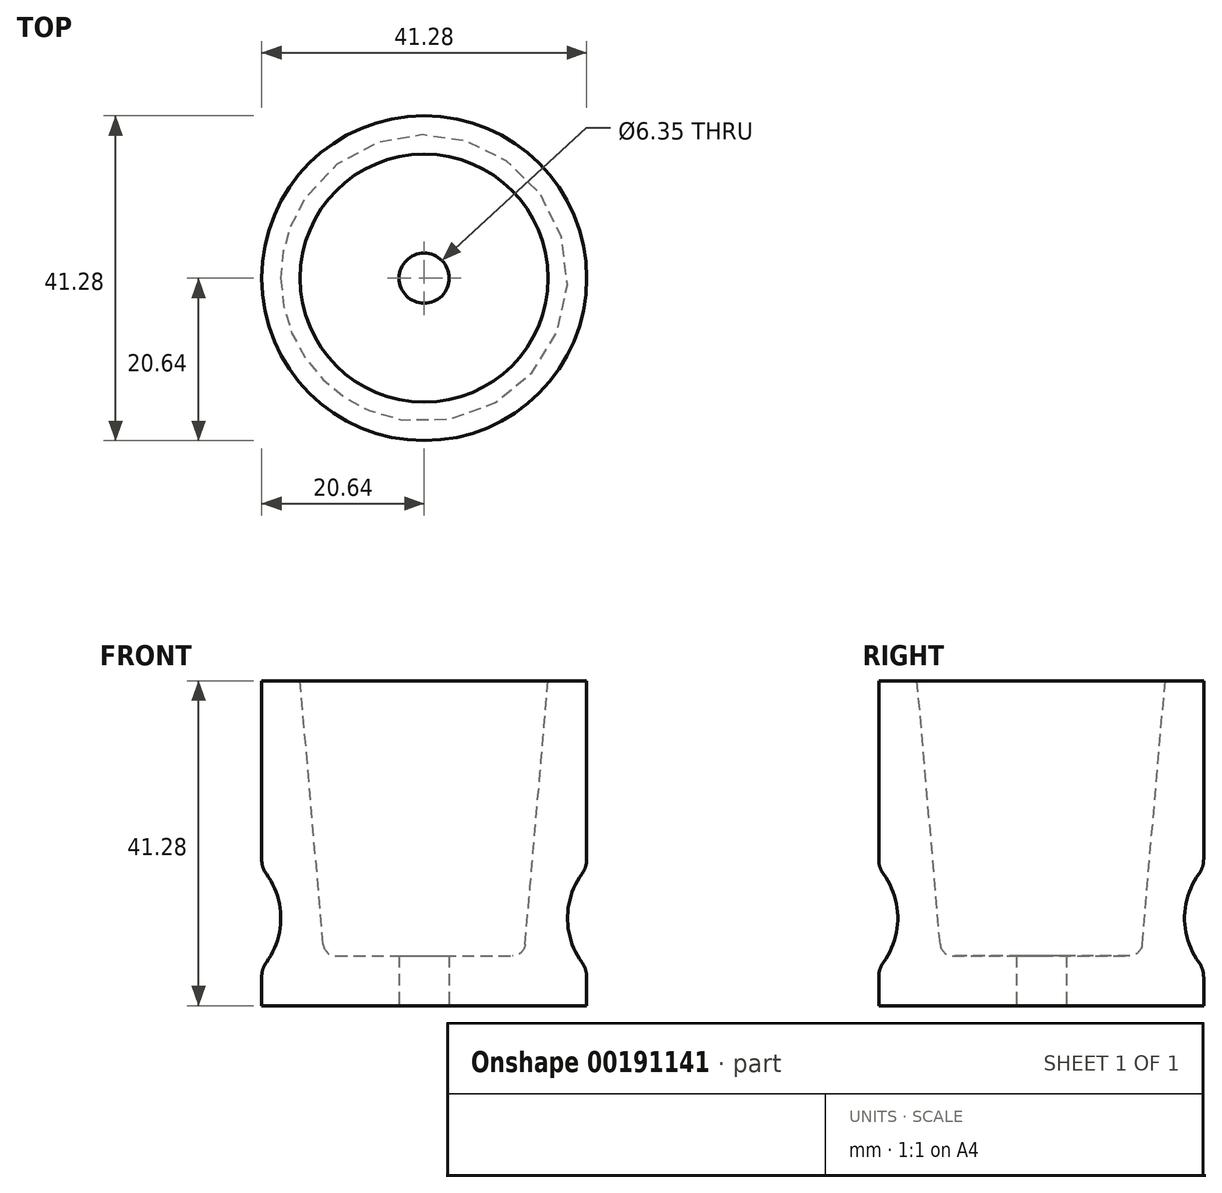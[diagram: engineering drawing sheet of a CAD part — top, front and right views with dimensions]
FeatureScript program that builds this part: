
annotation { "Feature Type Name" : "Feature", "Feature Type Description" : "" }
export const myFeature = defineFeature(function(context is Context, id is Id, definition is map)
    precondition{}
    {
        {
            var Q0;
            Q0=qCreatedBy(makeId("Front.planeOp"),FACE);
            var sketch = newSketch(context, id + "F0", { "sketchPlane" : qUnion([Q0])});
            skLineSegment(sketch, "E0", {"start": v(0, 0) * mm, "end": v(0, 84.8) * mm, "construction": true});
            skLineSegment(sketch, "E1", {"start": v(3.18, 0) * mm, "end": v(20.64, 0) * mm});
            skLineSegment(sketch, "E2", {"start": v(20.64, 41.28) * mm, "end": v(15.76, 41.28) * mm});
            skLineSegment(sketch, "E3", {"start": v(3.18, 6.35) * mm, "end": v(3.18, 0) * mm});
            skLineSegment(sketch, "E4", {"start": v(3.18, 6.35) * mm, "end": v(12.7, 6.35) * mm});
            skLineSegment(sketch, "E5", {"start": v(12.7, 6.35) * mm, "end": v(15.76, 41.28) * mm});
            skLineSegment(sketch, "E6", {"start": v(20.64, 0) * mm, "end": v(20.64, 4.76) * mm});
            skArc(sketch, "E7", {"start": v(20.64, 17.46) * mm, "mid": v(18.21, 11.11) * mm, "end": v(20.64, 4.76) * mm});
            skLineSegment(sketch, "E8", {"start": v(20.64, 41.28) * mm, "end": v(20.64, 17.46) * mm});
            skSolve(sketch);
        }
        {
            var Q0;
            Q0 = qSketchRegion(id + "F0", true);
            var Q1;
            Q1=sQuery(id+"F0.wireOp",EDGE,"E0");
            revolve(context, id + "F1", {"entities" : qUnion([Q0]), "axis" : qUnion([Q1]), "revolveType" : RevolveType.FULL});
        }
        {
            var Q0;
            Q0=makeQuery(id+"F1.opRevolve","SWEPT_EDGE",EDGE,{"disambiguationData":[OSD([sQuery(id+"F0.wireOp",EDGE,"E4"),sQuery(id+"F0.wireOp",EDGE,"E5")])]});
            fillet(context, id + "F2", {"entities" : qUnion([Q0]), "radius" : 1.59 * mm, "tangentPropagation" : true, "allowEdgeOverflow" : false});
        }
        {
            var Q0;
            Q0=makeQuery(id+"F1.opRevolve","SWEPT_EDGE",EDGE,{"disambiguationData":[OSD([sQuery(id+"F0.wireOp",EDGE,"E7"),sQuery(id+"F0.wireOp",EDGE,"E8")])]});
            var Q1;
            Q1=makeQuery(id+"F1.opRevolve","SWEPT_EDGE",EDGE,{"disambiguationData":[OSD([sQuery(id+"F0.wireOp",EDGE,"E6"),sQuery(id+"F0.wireOp",EDGE,"E7")])]});
            fillet(context, id + "F3", {"entities" : qUnion([Q0, Q1]), "radius" : 3.17 * mm, "tangentPropagation" : true, "allowEdgeOverflow" : false});
        }
    });
